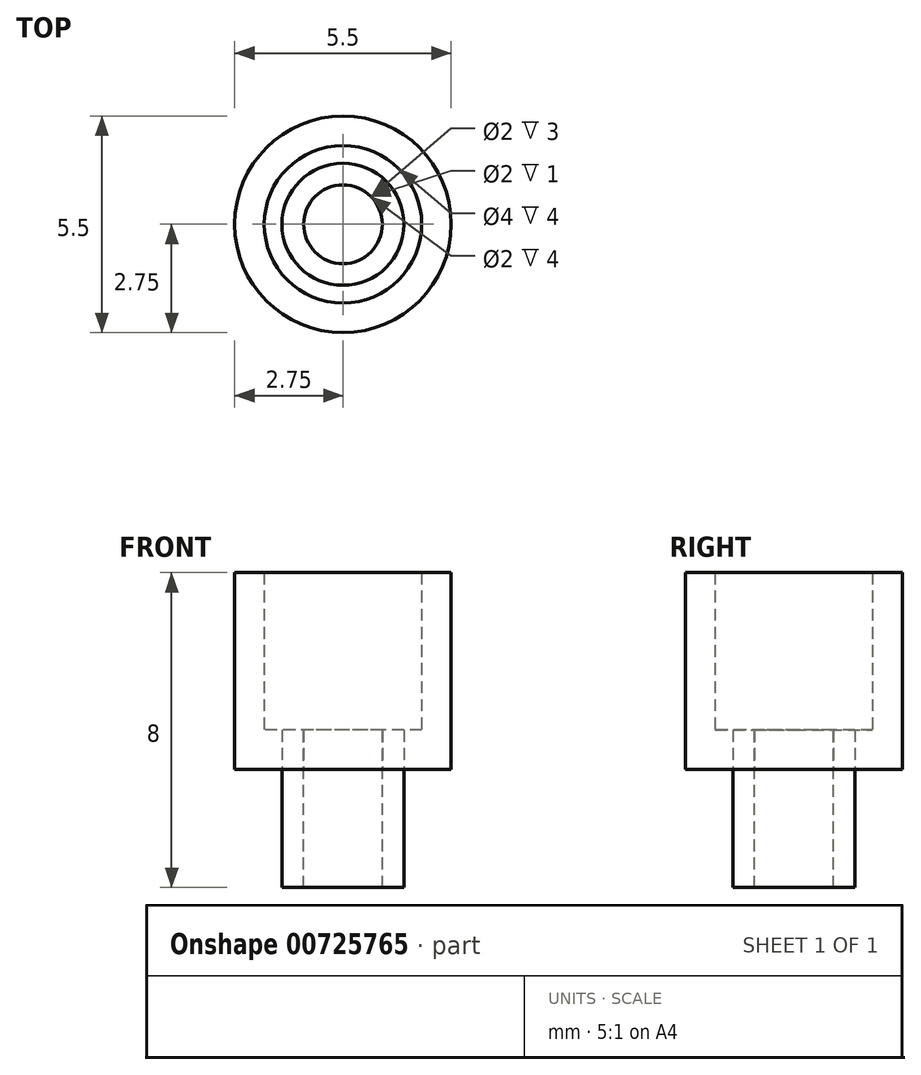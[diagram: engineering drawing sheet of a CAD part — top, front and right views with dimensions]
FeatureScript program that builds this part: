
annotation { "Feature Type Name" : "Feature", "Feature Type Description" : "" }
export const myFeature = defineFeature(function(context is Context, id is Id, definition is map)
    precondition{}
    {
        {
            var Q0;
            Q0=qCreatedBy(makeId("Top.planeOp"),FACE);
            var sketch = newSketch(context, id + "F0", { "sketchPlane" : qUnion([Q0])});
            skCircle(sketch, "E0", {"center": v(0, 0) * mm, "radius": 2 * mm});
            skCircle(sketch, "E1", {"center": v(0, 0) * mm, "radius": 2.75 * mm});
            skCircle(sketch, "E2", {"center": v(0, 0) * mm, "radius": 1.55 * mm});
            skCircle(sketch, "E3", {"center": v(0, 0) * mm, "radius": 1 * mm});
            skSolve(sketch);
        }
        {
            var Q0;
            Q0=makeQuery(id+"F0.imprint","IMPRINT",FACE,{"disambiguationData":[TD([[makeQuery(id+"F0.imprint","IMPRINT",EDGE,{"derivedFrom":sQuery(id+"F0.wireOp",EDGE,"E0")}),-1.0]])]});
            extrude(context, id + "F1", {"entities" : qUnion([Q0]), "depth" : 5 * mm, "offsetDistance" : 25 * mm});
        }
        {
            var Q0;
            Q0=makeQuery(id+"F0.imprint","IMPRINT",FACE,{"disambiguationData":[TD([[makeQuery(id+"F0.imprint","IMPRINT",EDGE,{"derivedFrom":sQuery(id+"F0.wireOp",EDGE,"E0")}),-1.0]])]});
            var Q1;
            Q1=makeQuery(id+"F0.imprint","IMPRINT",FACE,{"disambiguationData":[TD([[makeQuery(id+"F0.imprint","IMPRINT",EDGE,{"derivedFrom":sQuery(id+"F0.wireOp",EDGE,"E0")}),1.0]])]});
            extrude(context, id + "F2", {"entities" : qUnion([Q0, Q1]), "operationType" : NewBodyOperationType.ADD, "depth" : 1 * mm, "offsetDistance" : 25 * mm});
        }
        {
            var Q0;
            Q0=makeQuery(id+"F0.imprint","IMPRINT",FACE,{"disambiguationData":[TD([[makeQuery(id+"F0.imprint","IMPRINT",EDGE,{"derivedFrom":sQuery(id+"F0.wireOp",EDGE,"E2")}),1.0]])]});
            extrude(context, id + "F3", {"entities" : qUnion([Q0]), "oppositeDirection" : true, "depth" : 3 * mm, "offsetDistance" : 25 * mm});
        }
        {
            var Q0;
            Q0=makeQuery(id+"F0.imprint","IMPRINT",FACE,{"disambiguationData":[TD([[makeQuery(id+"F0.imprint","IMPRINT",EDGE,{"derivedFrom":sQuery(id+"F0.wireOp",EDGE,"E2")}),1.0]])]});
            extrude(context, id + "F4", {"entities" : qUnion([Q0]), "depth" : 1 * mm, "offsetDistance" : 25 * mm});
        }
    });
